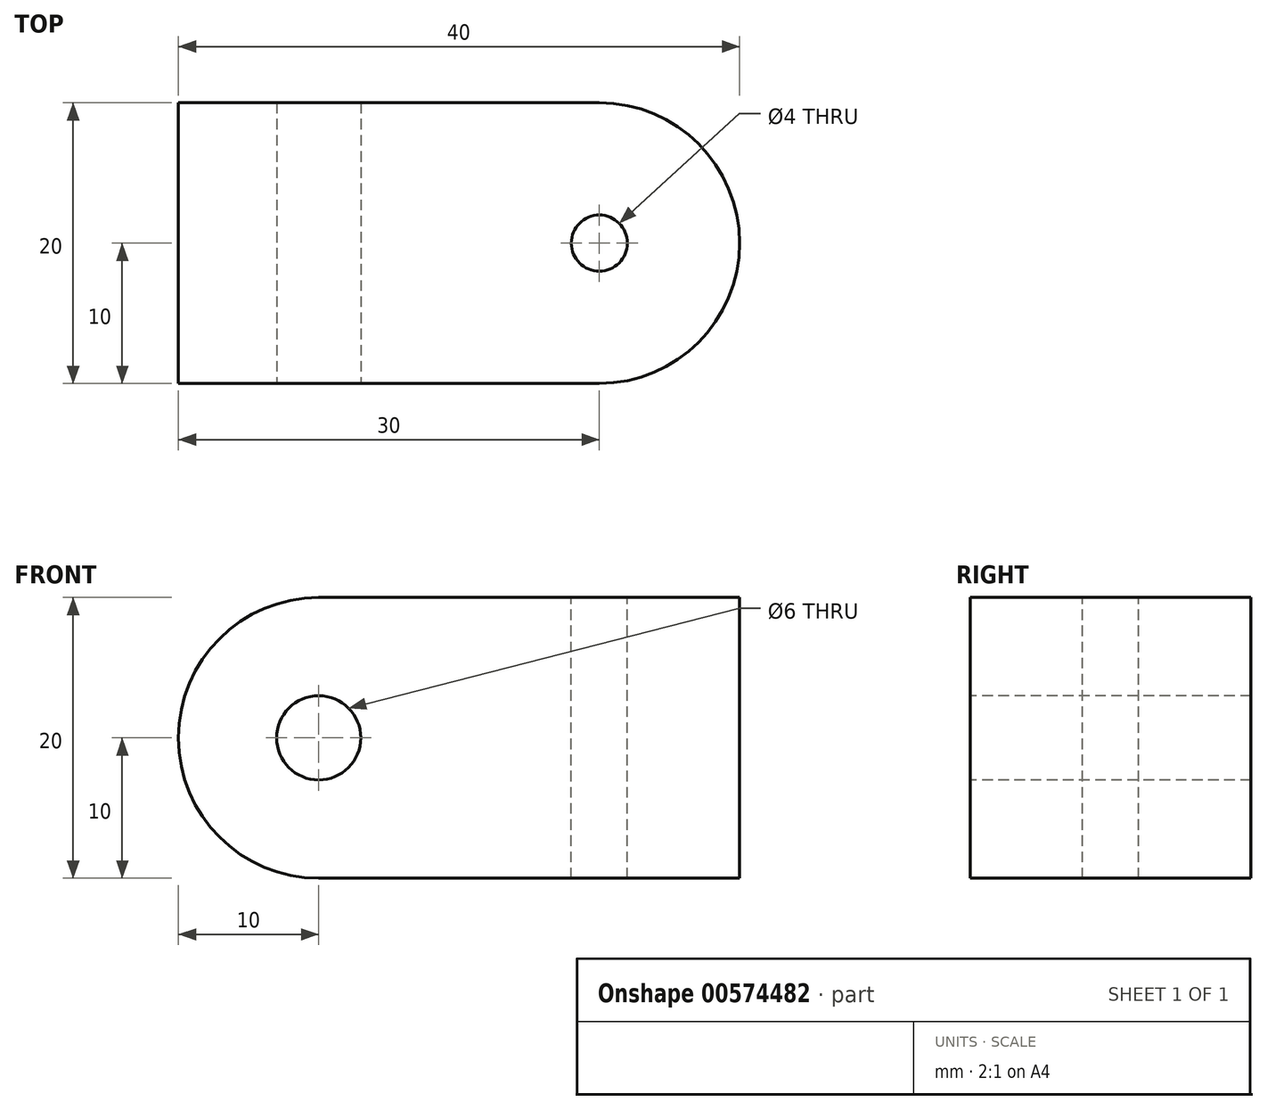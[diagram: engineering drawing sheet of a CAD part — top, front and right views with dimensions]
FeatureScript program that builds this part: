
annotation { "Feature Type Name" : "Feature", "Feature Type Description" : "" }
export const myFeature = defineFeature(function(context is Context, id is Id, definition is map)
    precondition{}
    {
        {
            var Q0;
            Q0=qCreatedBy(makeId("Top.planeOp"),FACE);
            var sketch = newSketch(context, id + "F0", { "sketchPlane" : qUnion([Q0])});
            skLineSegment(sketch, "E0.bottom", {"start": v(0, 0) * mm, "end": v(40, 0) * mm});
            skLineSegment(sketch, "E0.top", {"start": v(0, 20) * mm, "end": v(40, 20) * mm});
            skLineSegment(sketch, "E0.left", {"start": v(0, 0) * mm, "end": v(0, 20) * mm});
            skLineSegment(sketch, "E0.right", {"start": v(40, 0) * mm, "end": v(40, 20) * mm});
            skSolve(sketch);
        }
        {
            var Q0;
            Q0=makeQuery(id+"F0.imprint","IMPRINT",FACE,{"disambiguationData":[TD([[makeQuery(id+"F0.imprint","IMPRINT",EDGE,{"derivedFrom":sQuery(id+"F0.wireOp",EDGE,"E0.bottom")}),1.0]])]});
            extrude(context, id + "F1", {"entities" : qUnion([Q0]), "depth" : 20 * mm, "offsetDistance" : 25 * mm});
        }
        {
            var Q0;
            Q0=makeQuery(id+"F1.opExtrude","CAP_FACE",FACE,{"disambiguationData":[OSD([sQuery(id+"F0.wireOp",EDGE,"E0.bottom"),sQuery(id+"F0.wireOp",EDGE,"E0.top"),sQuery(id+"F0.wireOp",EDGE,"E0.left"),sQuery(id+"F0.wireOp",EDGE,"E0.right")])],"isStart":false});
            var sketch = newSketch(context, id + "F2", { "sketchPlane" : qUnion([Q0])});
            skPoint(sketch, "E1", {"position": v(30, 10) * mm});
            skSolve(sketch);
        }
        {
            var Q0;
            Q0=sQuery(id+"F2.wireOp",VERTEX,"E1");
            var Q1;
            Q1=makeQuery(id+"F1.opExtrude","SWEPT_BODY",BODY,{"disambiguationData":[OSD([sQuery(id+"F0.wireOp",EDGE,"E0.bottom"),sQuery(id+"F0.wireOp",EDGE,"E0.top"),sQuery(id+"F0.wireOp",EDGE,"E0.left"),sQuery(id+"F0.wireOp",EDGE,"E0.right")])]});
            hole(context, id + "F3", {"style" : HoleStyle.SIMPLE, "endStyle" : HoleEndStyle.THROUGH, "holeDiameter" : 4 * mm, "isTappedThrough" : true, "tappedDepth" : 12 * mm, "tapClearance" : 3, "locations" : qUnion([Q0]), "scope" : qUnion([Q1])});
        }
        {
            var Q0;
            Q0=makeQuery(id+"F1.opExtrude","SWEPT_FACE",FACE,{"disambiguationData":[OSD([sQuery(id+"F0.wireOp",EDGE,"E0.bottom")])]});
            var sketch = newSketch(context, id + "F4", { "sketchPlane" : qUnion([Q0])});
            skPoint(sketch, "E2", {"position": v(10, 10) * mm});
            skSolve(sketch);
        }
        {
            var Q0;
            Q0=sQuery(id+"F4.wireOp",VERTEX,"E2");
            var Q1;
            Q1=makeQuery(id+"F1.opExtrude","SWEPT_BODY",BODY,{"disambiguationData":[OSD([sQuery(id+"F0.wireOp",EDGE,"E0.bottom"),sQuery(id+"F0.wireOp",EDGE,"E0.top"),sQuery(id+"F0.wireOp",EDGE,"E0.left"),sQuery(id+"F0.wireOp",EDGE,"E0.right")])]});
            hole(context, id + "F5", {"style" : HoleStyle.SIMPLE, "endStyle" : HoleEndStyle.THROUGH, "holeDiameter" : 6 * mm, "isTappedThrough" : true, "tappedDepth" : 12 * mm, "tapClearance" : 3, "locations" : qUnion([Q0]), "scope" : qUnion([Q1])});
        }
        {
            var Q0;
            Q0=makeQuery(id+"F1.opExtrude","SWEPT_EDGE",EDGE,{"disambiguationData":[OSD([sQuery(id+"F0.wireOp",EDGE,"E0.bottom"),sQuery(id+"F0.wireOp",EDGE,"E0.right")])]});
            var Q1;
            Q1=makeQuery(id+"F1.opExtrude","SWEPT_EDGE",EDGE,{"disambiguationData":[OSD([sQuery(id+"F0.wireOp",EDGE,"E0.top"),sQuery(id+"F0.wireOp",EDGE,"E0.right")])]});
            fillet(context, id + "F6", {"entities" : qUnion([Q0, Q1]), "radius" : 10 * mm, "tangentPropagation" : true, "allowEdgeOverflow" : false});
        }
        {
            var Q0;
            Q0=makeQuery(id+"F1.opExtrude","CAP_EDGE",EDGE,{"disambiguationData":[OSD([sQuery(id+"F0.wireOp",EDGE,"E0.left")])],"isStart":true});
            var Q1;
            Q1=makeQuery(id+"F1.opExtrude","CAP_EDGE",EDGE,{"disambiguationData":[OSD([sQuery(id+"F0.wireOp",EDGE,"E0.left")])],"isStart":false});
            fillet(context, id + "F7", {"entities" : qUnion([Q0, Q1]), "radius" : 10 * mm, "tangentPropagation" : true, "allowEdgeOverflow" : false});
        }
    });
